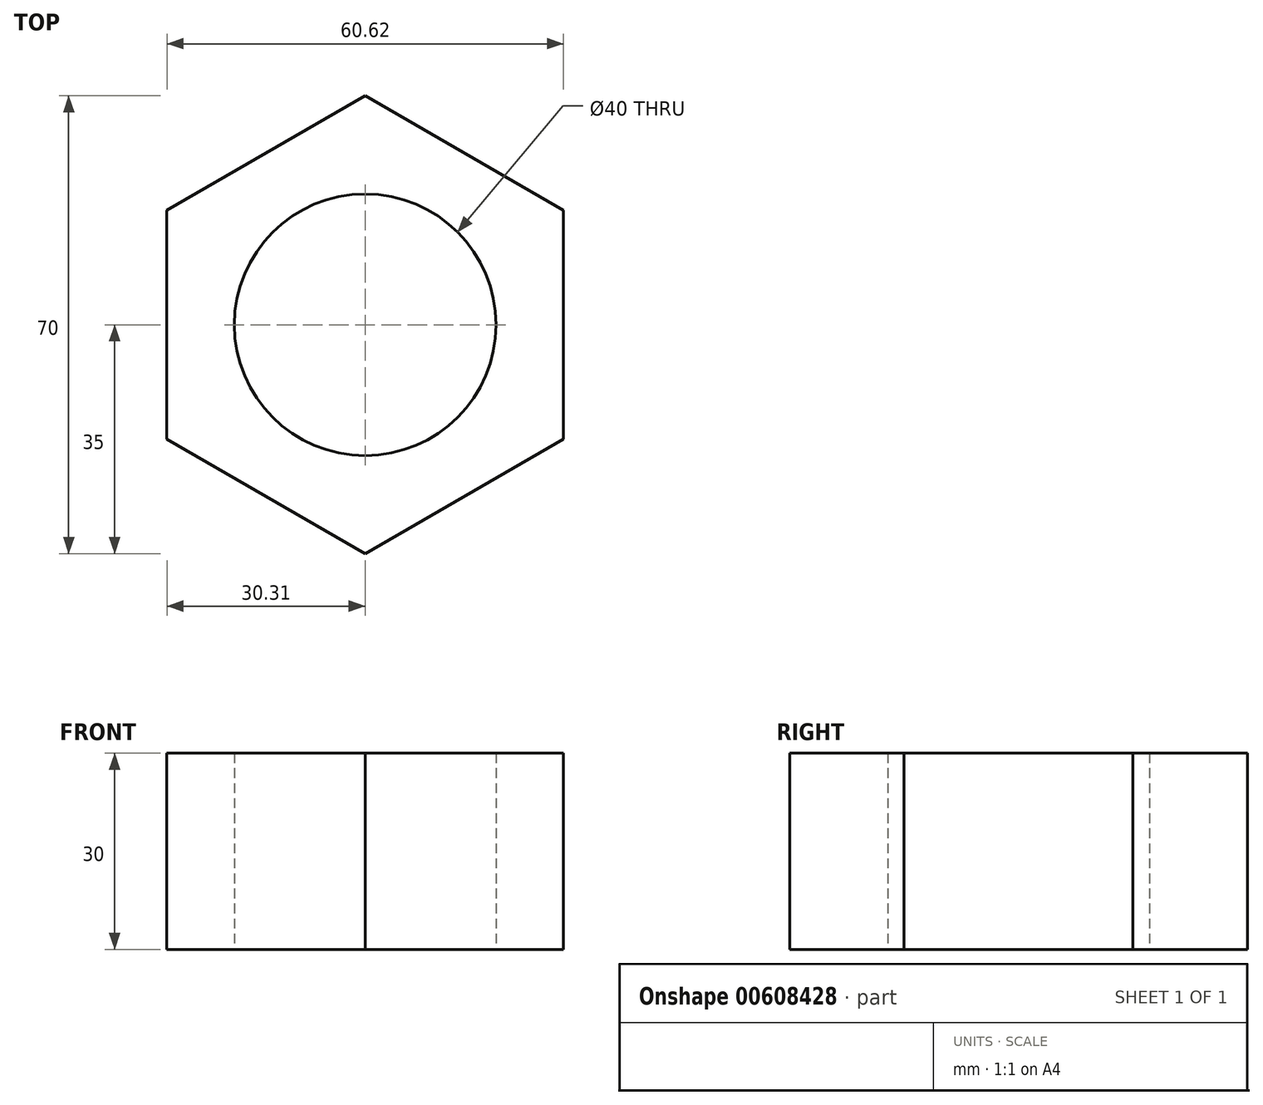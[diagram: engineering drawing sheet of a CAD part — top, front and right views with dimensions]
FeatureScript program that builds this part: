
annotation { "Feature Type Name" : "Feature", "Feature Type Description" : "" }
export const myFeature = defineFeature(function(context is Context, id is Id, definition is map)
    precondition{}
    {
        {
            var Q0;
            Q0=qCreatedBy(makeId("Top.planeOp"),FACE);
            var sketch = newSketch(context, id + "F0", { "sketchPlane" : qUnion([Q0])});
            skCircle(sketch, "E0.cCircle", {"center": v(0, 0) * mm, "radius": 35 * mm, "construction": true});
            skLineSegment(sketch, "E0.0", {"start": v(30.31, -17.5) * mm, "end": v(0, -35) * mm});
            skLineSegment(sketch, "E0.1", {"start": v(0, -35) * mm, "end": v(-30.31, -17.5) * mm});
            skLineSegment(sketch, "E0.2", {"start": v(-30.31, -17.5) * mm, "end": v(-30.31, 17.5) * mm});
            skLineSegment(sketch, "E0.3", {"start": v(-30.31, 17.5) * mm, "end": v(0, 35) * mm});
            skLineSegment(sketch, "E0.4", {"start": v(0, 35) * mm, "end": v(30.31, 17.5) * mm});
            skLineSegment(sketch, "E0.5", {"start": v(30.31, 17.5) * mm, "end": v(30.31, -17.5) * mm});
            skCircle(sketch, "E1", {"center": v(0, 0) * mm, "radius": 20 * mm});
            skSolve(sketch);
        }
        {
            var Q0;
            Q0 = qSketchRegion(id + "F0", true);
            extrude(context, id + "F1", {"entities" : qUnion([Q0]), "depth" : 30 * mm, "offsetDistance" : 25 * mm});
        }
    });
